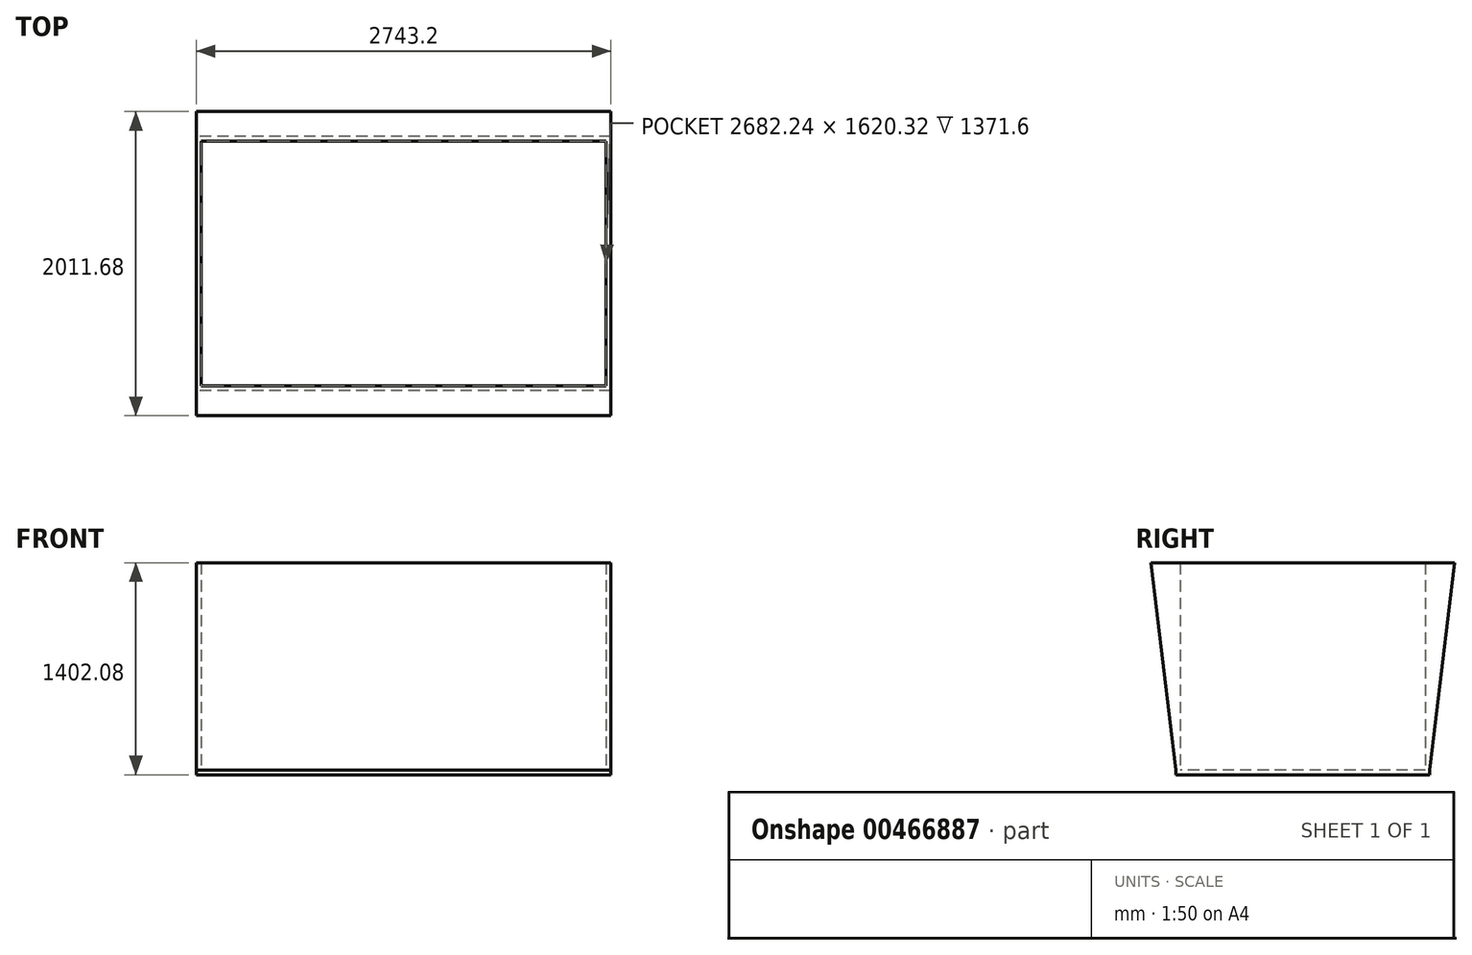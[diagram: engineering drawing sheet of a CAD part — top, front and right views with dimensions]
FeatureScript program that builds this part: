
annotation { "Feature Type Name" : "Feature", "Feature Type Description" : "" }
export const myFeature = defineFeature(function(context is Context, id is Id, definition is map)
    precondition{}
    {
        {
            var Q0;
            Q0=qCreatedBy(makeId("Right.planeOp"),FACE);
            var sketch = newSketch(context, id + "F0", { "sketchPlane" : qUnion([Q0])});
            skLineSegment(sketch, "E0", {"start": v(0, -1338.09) * mm, "end": v(-840.64, -1338.09) * mm});
            skLineSegment(sketch, "E1", {"start": v(0, 33.51) * mm, "end": v(-1005.84, 33.51) * mm});
            skLineSegment(sketch, "E2", {"start": v(-1005.84, 33.51) * mm, "end": v(-840.64, -1338.09) * mm});
            skLineSegment(sketch, "E3", {"start": v(0, 0) * mm, "end": v(0, -1338.09) * mm});
            skLineSegment(sketch, "E4.MirrorCS", {"start": v(0, 33.51) * mm, "end": v(1005.84, 33.51) * mm});
            skLineSegment(sketch, "E5.MirrorCS", {"start": v(0, -1338.09) * mm, "end": v(840.64, -1338.09) * mm});
            skLineSegment(sketch, "E6.MirrorCS", {"start": v(1005.84, 33.51) * mm, "end": v(840.64, -1338.09) * mm});
            skSolve(sketch);
        }
        {
            var Q0;
            Q0=makeQuery(id+"F0.imprint","IMPRINT",FACE,{"disambiguationData":[TD([[makeQuery(id+"F0.imprint","IMPRINT",EDGE,{"derivedFrom":sQuery(id+"F0.wireOp",EDGE,"E0")}),-1.0]])]});
            extrude(context, id + "F1", {"entities" : qUnion([Q0]), "depth" : 2743.2 * mm, "offsetDistance" : 30.48 * mm});
        }
        {
            var Q0;
            Q0=makeQuery(id+"F1.opExtrude","SWEPT_FACE",FACE,{"disambiguationData":[OSD([sQuery(id+"F0.wireOp",EDGE,"E0"),sQuery(id+"F0.wireOp",EDGE,"E5.MirrorCS")])]});
            var sketch = newSketch(context, id + "F2", { "sketchPlane" : qUnion([Q0])});
            skLineSegment(sketch, "E7.bottom", {"start": v(2712.72, -810.16) * mm, "end": v(30.48, -810.16) * mm});
            skLineSegment(sketch, "E7.top", {"start": v(2712.72, 810.16) * mm, "end": v(30.48, 810.16) * mm});
            skLineSegment(sketch, "E7.left", {"start": v(2712.72, -810.16) * mm, "end": v(2712.72, 810.16) * mm});
            skLineSegment(sketch, "E7.right", {"start": v(30.48, -810.16) * mm, "end": v(30.48, 810.16) * mm});
            skPoint(sketch, "E7.middle", {"position": v(1371.6, 0) * mm});
            skSolve(sketch);
        }
        {
            var Q0;
            Q0=makeQuery(id+"F2.imprint","IMPRINT",FACE,{"disambiguationData":[TD([[makeQuery(id+"F2.imprint","IMPRINT",EDGE,{"derivedFrom":sQuery(id+"F2.wireOp",EDGE,"E7.bottom")}),-1.0]])]});
            var Q1;
            Q1=makeQuery(id+"F1.opExtrude","SWEPT_FACE",FACE,{"disambiguationData":[OSD([sQuery(id+"F0.wireOp",EDGE,"E1"),sQuery(id+"F0.wireOp",EDGE,"E4.MirrorCS")])]});
            extrude(context, id + "F3", {"entities" : qUnion([Q0]), "operationType" : NewBodyOperationType.REMOVE, "endBound" : BoundingType.UP_TO_SURFACE, "oppositeDirection" : true, "depth" : 1524 * mm, "endBoundEntityFace" : qUnion([Q1]), "offsetDistance" : 30.48 * mm});
        }
        {
            var Q0;
            Q0=makeQuery(id+"F1.opExtrude","SWEPT_FACE",FACE,{"disambiguationData":[OSD([sQuery(id+"F0.wireOp",EDGE,"E0"),sQuery(id+"F0.wireOp",EDGE,"E5.MirrorCS")])]});
            var sketch = newSketch(context, id + "F4", { "sketchPlane" : qUnion([Q0])});
            skLineSegment(sketch, "E8.bottom", {"start": v(0, 840.64) * mm, "end": v(2743.2, 840.64) * mm});
            skLineSegment(sketch, "E8.top", {"start": v(0, -840.64) * mm, "end": v(2743.2, -840.64) * mm});
            skLineSegment(sketch, "E8.left", {"start": v(0, 840.64) * mm, "end": v(0, -840.64) * mm});
            skLineSegment(sketch, "E8.right", {"start": v(2743.2, 840.64) * mm, "end": v(2743.2, -840.64) * mm});
            skPoint(sketch, "E8.middle", {"position": v(1371.6, 0) * mm});
            skSolve(sketch);
        }
        {
            var Q0;
            Q0 = qSketchRegion(id + "F4", true);
            extrude(context, id + "F5", {"entities" : qUnion([Q0]), "operationType" : NewBodyOperationType.ADD, "depth" : 30.48 * mm, "offsetDistance" : 30.48 * mm});
        }
    });
